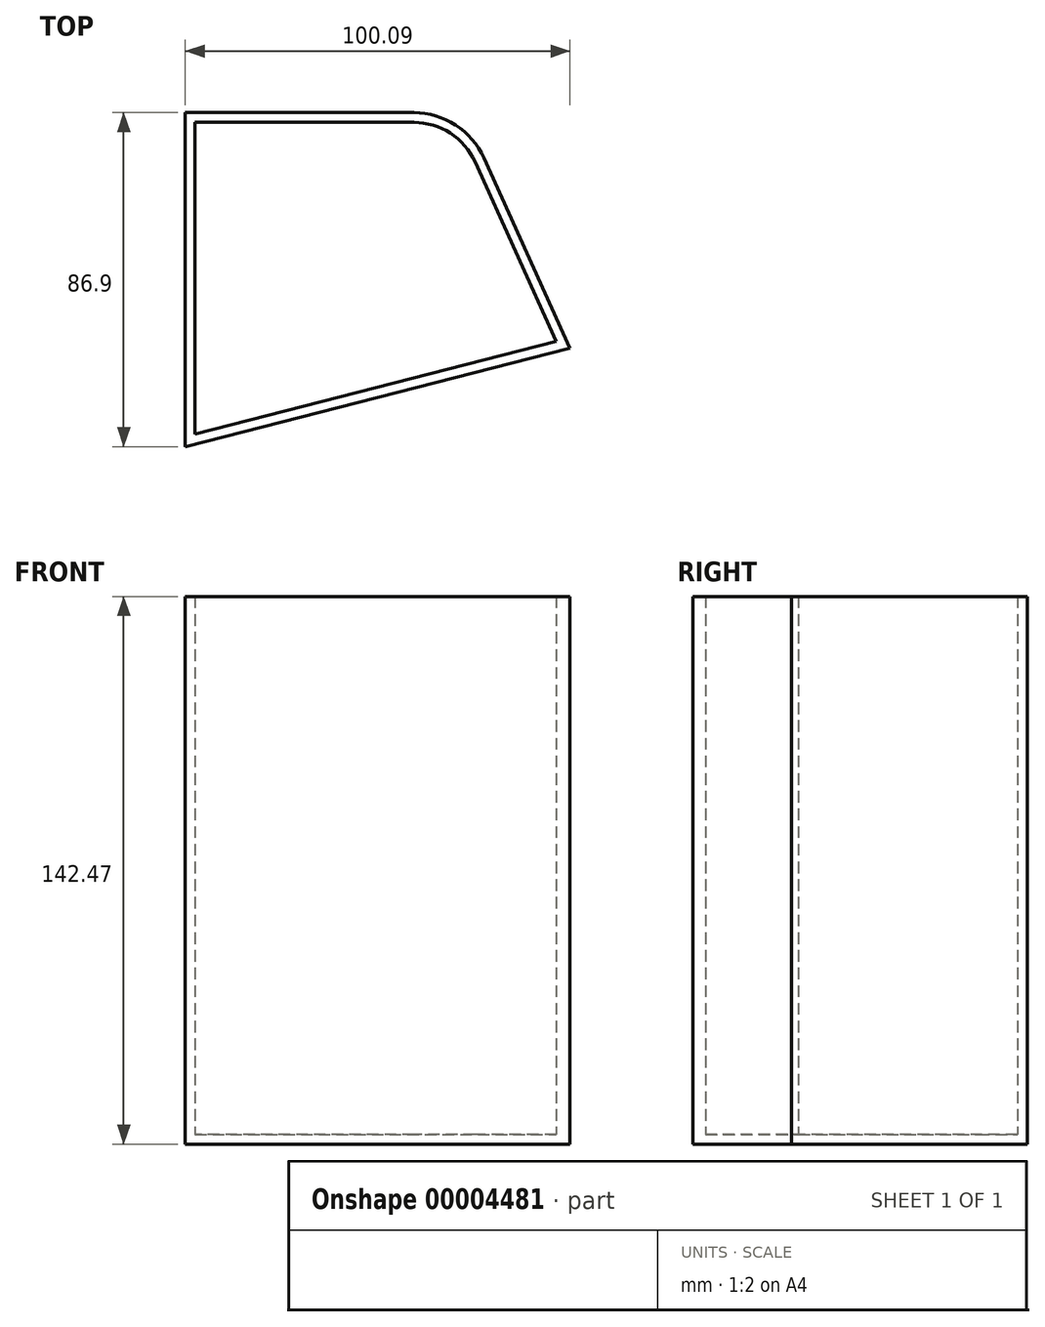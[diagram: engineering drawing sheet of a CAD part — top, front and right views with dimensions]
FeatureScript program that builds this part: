
annotation { "Feature Type Name" : "Feature", "Feature Type Description" : "" }
export const myFeature = defineFeature(function(context is Context, id is Id, definition is map)
    precondition{}
    {
        {
            var Q0;
            Q0=qCreatedBy(makeId("Top.planeOp"),FACE);
            var sketch = newSketch(context, id + "F0", { "sketchPlane" : qUnion([Q0])});
            skLineSegment(sketch, "E0", {"start": v(-27.84, 0) * mm, "end": v(-55.57, 61.24) * mm});
            skLineSegment(sketch, "E1", {"start": v(-55.57, 61.24) * mm, "end": v(-127.93, 61.24) * mm});
            skLineSegment(sketch, "E2", {"start": v(-127.93, 61.24) * mm, "end": v(-127.93, -25.66) * mm});
            skLineSegment(sketch, "E3", {"start": v(-127.93, -25.66) * mm, "end": v(-27.84, 0) * mm});
            skSolve(sketch);
        }
        {
            var Q0;
            Q0=makeQuery(id+"F0.imprint","IMPRINT",FACE,{"disambiguationData":[TD([[makeQuery(id+"F0.imprint","IMPRINT",EDGE,{"derivedFrom":sQuery(id+"F0.wireOp",EDGE,"E0")}),1.0]])]});
            extrude(context, id + "F1", {"entities" : qUnion([Q0]), "depth" : 142.47 * mm});
        }
        {
            var Q0;
            Q0=makeQuery(id+"F1.opExtrude","SWEPT_EDGE",EDGE,{"disambiguationData":[OSD([sQuery(id+"F0.wireOp",EDGE,"E0"),sQuery(id+"F0.wireOp",EDGE,"E1")])]});
            fillet(context, id + "F2", {"entities" : qUnion([Q0]), "radius" : 20 * mm, "tangentPropagation" : true, "allowEdgeOverflow" : false});
        }
        {
            var Q0;
            Q0=makeQuery(id+"F1.opExtrude","CAP_FACE",FACE,{"disambiguationData":[OSD([sQuery(id+"F0.wireOp",EDGE,"E0"),sQuery(id+"F0.wireOp",EDGE,"E1"),sQuery(id+"F0.wireOp",EDGE,"E2"),sQuery(id+"F0.wireOp",EDGE,"E3")])],"isStart":false});
            shell(context, id + "F3", {"entities" : qUnion([Q0]), "thickness" : 2.54 * mm});
        }
    });
